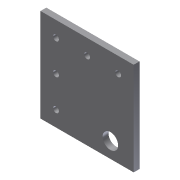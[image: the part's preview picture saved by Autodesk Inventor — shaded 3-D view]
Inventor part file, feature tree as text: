
AUTODESK INVENTOR PART (.ipt)
format: ipt  version: 2012 (Build 160160000, 160)  size: 95,232 bytes
history: native  units: in
note: dims shown in document units (in); Inventor stores cm internally (conversion verified against a paired STEP export)
features: extrude x3, sketch x3, pattern_linear x2
ambient origin geometry x8: Origin, YZ Plane, XZ Plane, XY Plane, X Axis, Y Axis, Z Axis, Center Point
bodies: Solid1 (feature_tree)
feature tree (8):
  extrude  "Extrusion1"  Depth=3.0in
  extrude  "Extrusion2"  Depth=0.5in
  extrude  "Extrusion3"  Depth=2.25in
  pattern_linear  "Rectangular Pattern1"  Spacing1=0.1875in  [1 undecoded]
  pattern_linear  "Rectangular Pattern2"  Spacing1=0.1875in  [1 undecoded]
  sketch  "Sketch1"  dims[d0=3.0in d1=3.0in]
  sketch  "Sketch2"  dims[d2=0.1875in d3=0.0in d4=0.5in]
  sketch  "Sketch3"  dims[d5=0.5in d6=2.25in d7=0.1875in d8=0.0in d9=0.1875in d10=0.5in d11=0.5in d12=0.1875in d13=0.0in d14=1.1811in d16=1.0in d17=1.1811in d19=1.0in]
note: 2 required parameter values undecoded (feature->parameter linkage not recoverable at this tier; creation-order binding heuristic only, values carry confidence <= 0.55)
